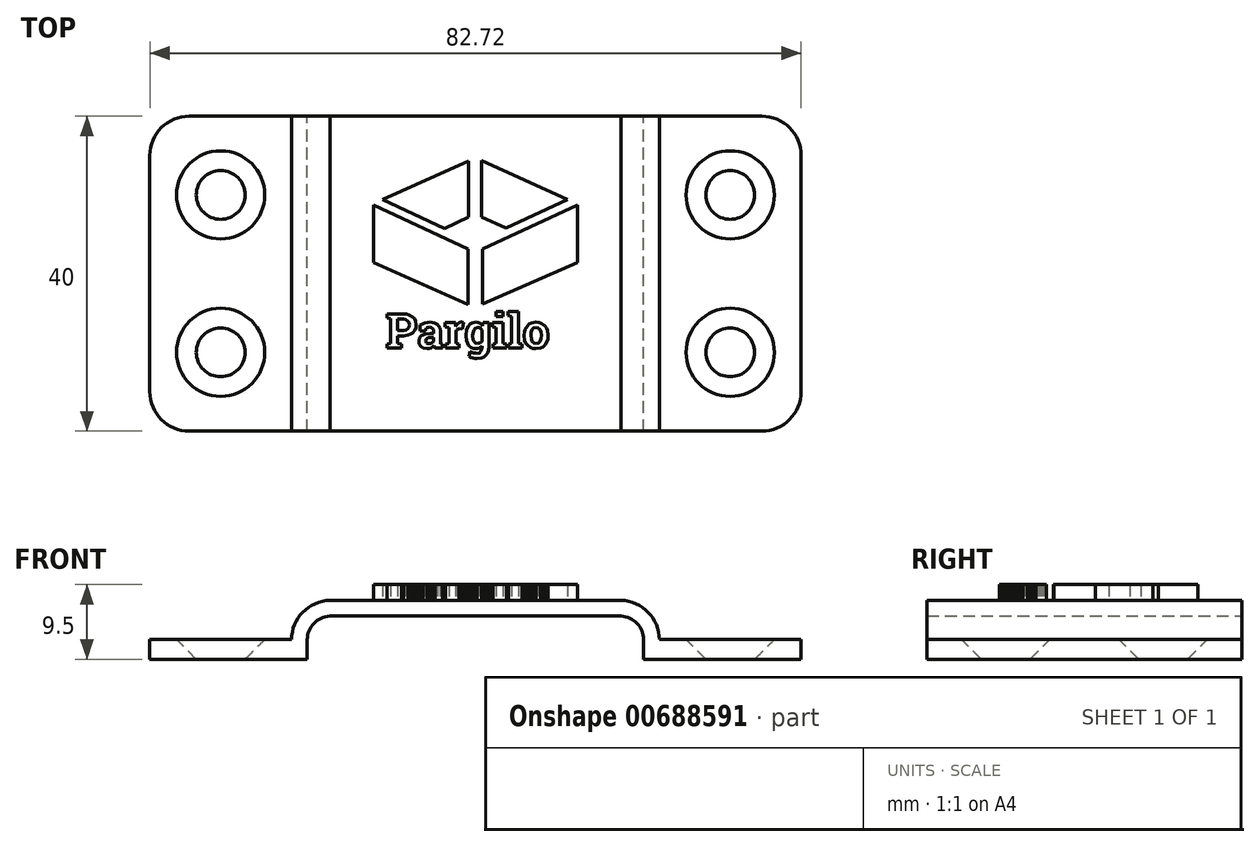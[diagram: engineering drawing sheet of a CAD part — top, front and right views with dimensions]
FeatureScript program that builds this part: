
annotation { "Feature Type Name" : "Feature", "Feature Type Description" : "" }
export const myFeature = defineFeature(function(context is Context, id is Id, definition is map)
    precondition{}
    {
        {
            var Q0;
            Q0=qCreatedBy(makeId("Front.planeOp"),FACE);
            var sketch = newSketch(context, id + "F0", { "sketchPlane" : qUnion([Q0])});
            skLineSegment(sketch, "E0.bottom", {"start": v(-41.36, 2.5) * mm, "end": v(-21.36, 2.5) * mm});
            skLineSegment(sketch, "E0.top", {"start": v(-41.36, 0) * mm, "end": v(-21.36, 0) * mm});
            skLineSegment(sketch, "E0.left", {"start": v(-41.36, 2.5) * mm, "end": v(-41.36, 0) * mm});
            skLineSegment(sketch, "E0.right", {"start": v(-21.36, 2.5) * mm, "end": v(-21.36, 0) * mm});
            skLineSegment(sketch, "E1.bottom", {"start": v(-18.5, 5.5) * mm, "end": v(0, 5.5) * mm});
            skLineSegment(sketch, "E1.top", {"start": v(-18.5, 7.5) * mm, "end": v(0, 7.5) * mm});
            skLineSegment(sketch, "E1.left", {"start": v(-18.5, 5.5) * mm, "end": v(-18.5, 7.5) * mm});
            skLineSegment(sketch, "E1.right", {"start": v(0, 5.5) * mm, "end": v(0, 7.5) * mm});
            skPoint(sketch, "E2", {"position": v(-18.33, 2.48) * mm});
            skArc(sketch, "E3", {"start": v(-18.5, 5.5) * mm, "mid": v(-20.53, 4.57) * mm, "end": v(-21.36, 2.5) * mm});
            skArc(sketch, "E4", {"start": v(-18.5, 7.5) * mm, "mid": v(-21.94, 5.98) * mm, "end": v(-23.36, 2.5) * mm});
            skLineSegment(sketch, "E5.MirrorCS", {"start": v(18.5, 5.5) * mm, "end": v(18.5, 7.5) * mm});
            skLineSegment(sketch, "E6.MirrorCS", {"start": v(21.36, 2.5) * mm, "end": v(21.36, 0) * mm});
            skLineSegment(sketch, "E7.MirrorCS", {"start": v(41.36, 2.5) * mm, "end": v(41.36, 0) * mm});
            skLineSegment(sketch, "E8.MirrorCS", {"start": v(18.5, 7.5) * mm, "end": v(0, 7.5) * mm});
            skArc(sketch, "E9.MirrorCS", {"start": v(18.5, 7.5) * mm, "mid": v(21.94, 5.98) * mm, "end": v(23.36, 2.5) * mm});
            skArc(sketch, "E10.MirrorCS", {"start": v(18.5, 5.5) * mm, "mid": v(20.53, 4.57) * mm, "end": v(21.36, 2.5) * mm});
            skLineSegment(sketch, "E11.MirrorCS", {"start": v(18.5, 5.5) * mm, "end": v(0, 5.5) * mm});
            skLineSegment(sketch, "E12.MirrorCS", {"start": v(41.36, 2.5) * mm, "end": v(21.36, 2.5) * mm});
            skLineSegment(sketch, "E13.MirrorCS", {"start": v(41.36, 0) * mm, "end": v(21.36, 0) * mm});
            skSolve(sketch);
        }
        {
            var Q0;
            Q0 = qSketchRegion(id + "F0", true);
            extrude(context, id + "F1", {"entities" : qUnion([Q0]), "depth" : 40 * mm, "offsetDistance" : 25 * mm});
        }
        {
            var Q0;
            Q0 = qSketchRegion(id + "F0", true);
            extrude(context, id + "F2", {"entities" : qUnion([Q0]), "operationType" : NewBodyOperationType.ADD, "depth" : 27 * mm, "offsetDistance" : 25 * mm});
        }
        {
            var Q0;
            Q0=makeQuery(id+"F1.opExtrude","SWEPT_FACE",FACE,{"disambiguationData":[OSD([sQuery(id+"F0.wireOp",EDGE,"E0.bottom")])]});
            var sketch = newSketch(context, id + "F3", { "sketchPlane" : qUnion([Q0])});
            skPoint(sketch, "E14", {"position": v(-32.36, -10) * mm});
            skPoint(sketch, "E15", {"position": v(-32.36, -30) * mm});
            skPoint(sketch, "E16.MirrorP", {"position": v(32.36, -10) * mm});
            skPoint(sketch, "E17.MirrorP", {"position": v(32.36, -30) * mm});
            skSolve(sketch);
        }
        {
            var Q0;
            Q0=sQuery(id+"F3.wireOp",VERTEX,"E14");
            var Q1;
            Q1=sQuery(id+"F3.wireOp",VERTEX,"E15");
            var Q2;
            Q2=sQuery(id+"F3.wireOp",VERTEX,"E17.MirrorP");
            var Q3;
            Q3=sQuery(id+"F3.wireOp",VERTEX,"E16.MirrorP");
            var Q4;
            Q4=makeQuery(id+"F1.opExtrude","SWEPT_BODY",BODY,{"disambiguationData":[OSD([sQuery(id+"F0.wireOp",EDGE,"E0.bottom"),sQuery(id+"F0.wireOp",EDGE,"E0.top"),sQuery(id+"F0.wireOp",EDGE,"E0.left"),sQuery(id+"F0.wireOp",EDGE,"E0.right"),sQuery(id+"F0.wireOp",EDGE,"E1.bottom"),sQuery(id+"F0.wireOp",EDGE,"E1.top"),sQuery(id+"F0.wireOp",EDGE,"E3"),sQuery(id+"F0.wireOp",EDGE,"E4"),sQuery(id+"F0.wireOp",EDGE,"E6.MirrorCS"),sQuery(id+"F0.wireOp",EDGE,"E7.MirrorCS"),sQuery(id+"F0.wireOp",EDGE,"E8.MirrorCS"),sQuery(id+"F0.wireOp",EDGE,"E9.MirrorCS"),sQuery(id+"F0.wireOp",EDGE,"E10.MirrorCS"),sQuery(id+"F0.wireOp",EDGE,"E11.MirrorCS"),sQuery(id+"F0.wireOp",EDGE,"E12.MirrorCS"),sQuery(id+"F0.wireOp",EDGE,"E13.MirrorCS")])]});
            hole(context, id + "F4", {"style" : HoleStyle.C_SINK, "endStyle" : HoleEndStyle.THROUGH, "standardTappedOrClearance" : lookupTablePath({ "standard" : "ISO", "size" : "5", "type" : "Drilled" }), "standardBlindInLast" : lookupTablePath({ "standard" : "ISO", "size" : "5", "type" : "Drilled" }), "holeDiameter" : 5 * mm, "cSinkDiameter" : 11.2 * mm, "cSinkAngle" : 90 * degree, "majorDiameter" : 5 * mm, "isTappedThrough" : true, "tappedDepth" : 12 * mm, "tapClearance" : 3, "locations" : qUnion([Q0, Q1, Q2, Q3]), "scope" : qUnion([Q4])});
        }
        {
            var Q0;
            Q0=makeQuery(id+"F1.opExtrude","CAP_EDGE",EDGE,{"disambiguationData":[OSD([sQuery(id+"F0.wireOp",EDGE,"E0.left")])],"isStart":false});
            var Q1;
            Q1=makeQuery(id+"F1.opExtrude","CAP_EDGE",EDGE,{"disambiguationData":[OSD([sQuery(id+"F0.wireOp",EDGE,"E7.MirrorCS")])],"isStart":false});
            var Q2;
            Q2=makeQuery(id+"F1.opExtrude","CAP_EDGE",EDGE,{"disambiguationData":[OSD([sQuery(id+"F0.wireOp",EDGE,"E7.MirrorCS")])],"isStart":true});
            var Q3;
            Q3=makeQuery(id+"F1.opExtrude","CAP_EDGE",EDGE,{"disambiguationData":[OSD([sQuery(id+"F0.wireOp",EDGE,"E0.left")])],"isStart":true});
            fillet(context, id + "F5", {"entities" : qUnion([Q0, Q1, Q2, Q3]), "radius" : 5 * mm, "tangentPropagation" : true, "allowEdgeOverflow" : false});
        }
        {
            var Q0;
            Q0=makeQuery(id+"F1.opExtrude","SWEPT_FACE",FACE,{"disambiguationData":[OSD([sQuery(id+"F0.wireOp",EDGE,"E1.top"),sQuery(id+"F0.wireOp",EDGE,"E8.MirrorCS")])]});
            var sketch = newSketch(context, id + "F6", { "sketchPlane" : qUnion([Q0])});
            skLineSegment(sketch, "E18", {"start": v(-12.95, -11.28) * mm, "end": v(-12.95, -18.58) * mm});
            skLineSegment(sketch, "E19", {"start": v(7.05, -27.83) * mm, "end": v(7.05, -27.9) * mm});
            skLineSegment(sketch, "E20", {"start": v(7.2, -27.12) * mm, "end": v(7.08, -27.48) * mm});
            skLineSegment(sketch, "E21", {"start": v(7.08, -27.48) * mm, "end": v(7.05, -27.83) * mm});
            skLineSegment(sketch, "E22", {"start": v(7.7, -26.85) * mm, "end": v(7.38, -26.94) * mm});
            skLineSegment(sketch, "E23", {"start": v(7.38, -26.94) * mm, "end": v(7.2, -27.12) * mm});
            skLineSegment(sketch, "E24", {"start": v(8.2, -27.12) * mm, "end": v(7.97, -26.9) * mm});
            skLineSegment(sketch, "E25", {"start": v(7.97, -26.9) * mm, "end": v(7.7, -26.85) * mm});
            skLineSegment(sketch, "E26", {"start": v(8.36, -27.83) * mm, "end": v(8.31, -27.4) * mm});
            skLineSegment(sketch, "E27", {"start": v(8.31, -27.4) * mm, "end": v(8.2, -27.12) * mm});
            skLineSegment(sketch, "E28", {"start": v(8.36, -27.9) * mm, "end": v(8.36, -27.83) * mm});
            skLineSegment(sketch, "E29", {"start": v(8.2, -28.6) * mm, "end": v(8.33, -28.25) * mm});
            skLineSegment(sketch, "E30", {"start": v(8.33, -28.25) * mm, "end": v(8.36, -27.9) * mm});
            skLineSegment(sketch, "E31", {"start": v(7.71, -28.87) * mm, "end": v(8.03, -28.79) * mm});
            skLineSegment(sketch, "E32", {"start": v(8.03, -28.79) * mm, "end": v(8.2, -28.6) * mm});
            skLineSegment(sketch, "E33", {"start": v(7.2, -28.6) * mm, "end": v(7.44, -28.82) * mm});
            skLineSegment(sketch, "E34", {"start": v(7.44, -28.82) * mm, "end": v(7.71, -28.87) * mm});
            skLineSegment(sketch, "E35", {"start": v(7.05, -27.9) * mm, "end": v(7.1, -28.33) * mm});
            skLineSegment(sketch, "E36", {"start": v(7.1, -28.33) * mm, "end": v(7.2, -28.6) * mm});
            skLineSegment(sketch, "E37", {"start": v(6.18, -27.9) * mm, "end": v(6.18, -27.83) * mm});
            skLineSegment(sketch, "E38", {"start": v(6.58, -29.08) * mm, "end": v(6.39, -28.8) * mm});
            skLineSegment(sketch, "E39", {"start": v(6.39, -28.8) * mm, "end": v(6.25, -28.48) * mm});
            skLineSegment(sketch, "E40", {"start": v(6.25, -28.48) * mm, "end": v(6.18, -27.9) * mm});
            skLineSegment(sketch, "E41", {"start": v(7.71, -29.54) * mm, "end": v(7.33, -29.5) * mm});
            skLineSegment(sketch, "E42", {"start": v(7.33, -29.5) * mm, "end": v(7, -29.4) * mm});
            skLineSegment(sketch, "E43", {"start": v(7, -29.4) * mm, "end": v(6.58, -29.08) * mm});
            skLineSegment(sketch, "E44", {"start": v(8.83, -29.08) * mm, "end": v(8.58, -29.3) * mm});
            skLineSegment(sketch, "E45", {"start": v(8.58, -29.3) * mm, "end": v(8.28, -29.45) * mm});
            skLineSegment(sketch, "E46", {"start": v(8.28, -29.45) * mm, "end": v(7.71, -29.54) * mm});
            skLineSegment(sketch, "E47", {"start": v(9.24, -27.9) * mm, "end": v(9.2, -28.28) * mm});
            skLineSegment(sketch, "E48", {"start": v(9.2, -28.28) * mm, "end": v(9.11, -28.62) * mm});
            skLineSegment(sketch, "E49", {"start": v(9.11, -28.62) * mm, "end": v(8.83, -29.08) * mm});
            skLineSegment(sketch, "E50", {"start": v(9.24, -27.83) * mm, "end": v(9.24, -27.9) * mm});
            skLineSegment(sketch, "E51", {"start": v(8.83, -26.64) * mm, "end": v(9.03, -26.92) * mm});
            skLineSegment(sketch, "E52", {"start": v(9.03, -26.92) * mm, "end": v(9.16, -27.24) * mm});
            skLineSegment(sketch, "E53", {"start": v(9.16, -27.24) * mm, "end": v(9.24, -27.83) * mm});
            skLineSegment(sketch, "E54", {"start": v(7.7, -26.17) * mm, "end": v(8.08, -26.21) * mm});
            skLineSegment(sketch, "E55", {"start": v(8.08, -26.21) * mm, "end": v(8.41, -26.32) * mm});
            skLineSegment(sketch, "E56", {"start": v(8.41, -26.32) * mm, "end": v(8.83, -26.64) * mm});
            skLineSegment(sketch, "E57", {"start": v(6.58, -26.64) * mm, "end": v(6.83, -26.42) * mm});
            skLineSegment(sketch, "E58", {"start": v(6.83, -26.42) * mm, "end": v(7.13, -26.26) * mm});
            skLineSegment(sketch, "E59", {"start": v(7.13, -26.26) * mm, "end": v(7.7, -26.17) * mm});
            skLineSegment(sketch, "E60", {"start": v(6.18, -27.83) * mm, "end": v(6.2, -27.44) * mm});
            skLineSegment(sketch, "E61", {"start": v(6.2, -27.44) * mm, "end": v(6.3, -27.1) * mm});
            skLineSegment(sketch, "E62", {"start": v(6.3, -27.1) * mm, "end": v(6.58, -26.64) * mm});
            skLineSegment(sketch, "E63", {"start": v(4.6, -25.42) * mm, "end": v(4.12, -25.33) * mm});
            skLineSegment(sketch, "E64", {"start": v(4.6, -28.86) * mm, "end": v(4.6, -25.42) * mm});
            skLineSegment(sketch, "E65", {"start": v(4.17, -28.95) * mm, "end": v(4.6, -28.86) * mm});
            skLineSegment(sketch, "E66", {"start": v(4.17, -29.48) * mm, "end": v(4.17, -28.95) * mm});
            skLineSegment(sketch, "E67", {"start": v(5.9, -29.48) * mm, "end": v(4.17, -29.48) * mm});
            skLineSegment(sketch, "E68", {"start": v(5.9, -28.95) * mm, "end": v(5.9, -29.48) * mm});
            skLineSegment(sketch, "E69", {"start": v(5.47, -28.86) * mm, "end": v(5.9, -28.95) * mm});
            skLineSegment(sketch, "E70", {"start": v(5.47, -24.8) * mm, "end": v(5.47, -28.86) * mm});
            skLineSegment(sketch, "E71", {"start": v(4.12, -24.8) * mm, "end": v(5.47, -24.8) * mm});
            skLineSegment(sketch, "E72", {"start": v(4.12, -25.33) * mm, "end": v(4.12, -24.8) * mm});
            skLineSegment(sketch, "E73", {"start": v(3.5, -24.8) * mm, "end": v(3.5, -25.46) * mm});
            skLineSegment(sketch, "E74", {"start": v(2.63, -24.8) * mm, "end": v(3.5, -24.8) * mm});
            skLineSegment(sketch, "E75", {"start": v(2.63, -25.46) * mm, "end": v(2.63, -24.8) * mm});
            skLineSegment(sketch, "E76", {"start": v(3.5, -25.46) * mm, "end": v(2.63, -25.46) * mm});
            skLineSegment(sketch, "E77", {"start": v(2.21, -29.48) * mm, "end": v(2.21, -28.95) * mm});
            skLineSegment(sketch, "E78", {"start": v(3.93, -29.48) * mm, "end": v(2.21, -29.48) * mm});
            skLineSegment(sketch, "E79", {"start": v(3.93, -28.95) * mm, "end": v(3.93, -29.48) * mm});
            skLineSegment(sketch, "E80", {"start": v(3.5, -28.86) * mm, "end": v(3.93, -28.95) * mm});
            skLineSegment(sketch, "E81", {"start": v(3.5, -26.24) * mm, "end": v(3.5, -28.86) * mm});
            skLineSegment(sketch, "E82", {"start": v(2.17, -26.24) * mm, "end": v(3.5, -26.24) * mm});
            skLineSegment(sketch, "E83", {"start": v(2.17, -26.76) * mm, "end": v(2.17, -26.24) * mm});
            skLineSegment(sketch, "E84", {"start": v(2.63, -26.85) * mm, "end": v(2.17, -26.76) * mm});
            skLineSegment(sketch, "E85", {"start": v(2.63, -28.86) * mm, "end": v(2.63, -26.85) * mm});
            skLineSegment(sketch, "E86", {"start": v(2.21, -28.95) * mm, "end": v(2.63, -28.86) * mm});
            skLineSegment(sketch, "E87", {"start": v(-0.34, -27.88) * mm, "end": v(-0.34, -27.95) * mm});
            skLineSegment(sketch, "E88", {"start": v(-0.2, -27.14) * mm, "end": v(-0.31, -27.51) * mm});
            skLineSegment(sketch, "E89", {"start": v(-0.31, -27.51) * mm, "end": v(-0.34, -27.88) * mm});
            skLineSegment(sketch, "E90", {"start": v(0.28, -26.86) * mm, "end": v(-0.03, -26.95) * mm});
            skLineSegment(sketch, "E91", {"start": v(-0.03, -26.95) * mm, "end": v(-0.2, -27.14) * mm});
            skLineSegment(sketch, "E92", {"start": v(0.61, -26.94) * mm, "end": v(0.44, -26.87) * mm});
            skLineSegment(sketch, "E93", {"start": v(0.44, -26.87) * mm, "end": v(0.28, -26.86) * mm});
            skLineSegment(sketch, "E94", {"start": v(0.84, -27.16) * mm, "end": v(0.72, -27.02) * mm});
            skLineSegment(sketch, "E95", {"start": v(0.72, -27.02) * mm, "end": v(0.61, -26.94) * mm});
            skLineSegment(sketch, "E96", {"start": v(0.84, -28.57) * mm, "end": v(0.84, -27.16) * mm});
            skLineSegment(sketch, "E97", {"start": v(0.61, -28.79) * mm, "end": v(0.75, -28.68) * mm});
            skLineSegment(sketch, "E98", {"start": v(0.75, -28.68) * mm, "end": v(0.84, -28.57) * mm});
            skLineSegment(sketch, "E99", {"start": v(0.27, -28.86) * mm, "end": v(0.48, -28.84) * mm});
            skLineSegment(sketch, "E100", {"start": v(0.48, -28.84) * mm, "end": v(0.61, -28.79) * mm});
            skLineSegment(sketch, "E101", {"start": v(-0.2, -28.62) * mm, "end": v(0.02, -28.81) * mm});
            skLineSegment(sketch, "E102", {"start": v(0.02, -28.81) * mm, "end": v(0.27, -28.86) * mm});
            skLineSegment(sketch, "E103", {"start": v(-0.34, -27.95) * mm, "end": v(-0.3, -28.37) * mm});
            skLineSegment(sketch, "E104", {"start": v(-0.3, -28.37) * mm, "end": v(-0.2, -28.62) * mm});
            skLineSegment(sketch, "E105", {"start": v(-4.15, -28.95) * mm, "end": v(-4.15, -29.48) * mm});
            skLineSegment(sketch, "E106", {"start": v(-4.42, -28.92) * mm, "end": v(-4.15, -28.95) * mm});
            skLineSegment(sketch, "E107", {"start": v(-4.43, -28.8) * mm, "end": v(-4.43, -28.86) * mm});
            skLineSegment(sketch, "E108", {"start": v(-4.43, -28.86) * mm, "end": v(-4.42, -28.92) * mm});
            skLineSegment(sketch, "E109", {"start": v(-4.43, -28.65) * mm, "end": v(-4.43, -28.73) * mm});
            skLineSegment(sketch, "E110", {"start": v(-4.43, -28.73) * mm, "end": v(-4.43, -28.8) * mm});
            skLineSegment(sketch, "E111", {"start": v(-4.43, -27.31) * mm, "end": v(-4.43, -28.65) * mm});
            skLineSegment(sketch, "E112", {"start": v(-4.8, -26.47) * mm, "end": v(-4.5, -26.88) * mm});
            skLineSegment(sketch, "E113", {"start": v(-4.5, -26.88) * mm, "end": v(-4.43, -27.31) * mm});
            skLineSegment(sketch, "E114", {"start": v(-5.79, -26.17) * mm, "end": v(-5.18, -26.27) * mm});
            skLineSegment(sketch, "E115", {"start": v(-5.18, -26.27) * mm, "end": v(-4.8, -26.47) * mm});
            skLineSegment(sketch, "E116", {"start": v(-6.46, -26.29) * mm, "end": v(-6.1, -26.2) * mm});
            skLineSegment(sketch, "E117", {"start": v(-6.1, -26.2) * mm, "end": v(-5.79, -26.17) * mm});
            skLineSegment(sketch, "E118", {"start": v(-7.01, -26.56) * mm, "end": v(-6.72, -26.4) * mm});
            skLineSegment(sketch, "E119", {"start": v(-6.72, -26.4) * mm, "end": v(-6.46, -26.29) * mm});
            skLineSegment(sketch, "E120", {"start": v(-7.02, -27.28) * mm, "end": v(-7.01, -26.56) * mm});
            skLineSegment(sketch, "E121", {"start": v(-4.15, -29.48) * mm, "end": v(-5.16, -29.48) * mm});
            skLineSegment(sketch, "E122", {"start": v(-5.92, -28.9) * mm, "end": v(-5.71, -28.87) * mm});
            skLineSegment(sketch, "E123", {"start": v(-5.71, -28.87) * mm, "end": v(-5.56, -28.8) * mm});
            skLineSegment(sketch, "E124", {"start": v(-5.56, -28.8) * mm, "end": v(-5.4, -28.7) * mm});
            skLineSegment(sketch, "E125", {"start": v(-5.4, -28.7) * mm, "end": v(-5.3, -28.6) * mm});
            skLineSegment(sketch, "E126", {"start": v(-5.3, -28.6) * mm, "end": v(-5.3, -28.1) * mm});
            skLineSegment(sketch, "E127", {"start": v(-5.3, -28.1) * mm, "end": v(-5.76, -28.1) * mm});
            skLineSegment(sketch, "E128", {"start": v(-5.76, -28.1) * mm, "end": v(-6.03, -28.14) * mm});
            skLineSegment(sketch, "E129", {"start": v(-6.03, -28.14) * mm, "end": v(-6.18, -28.23) * mm});
            skLineSegment(sketch, "E130", {"start": v(-6.18, -28.23) * mm, "end": v(-6.3, -28.4) * mm});
            skLineSegment(sketch, "E131", {"start": v(-6.3, -28.4) * mm, "end": v(-6.32, -28.54) * mm});
            skLineSegment(sketch, "E132", {"start": v(-6.32, -28.54) * mm, "end": v(-6.29, -28.7) * mm});
            skLineSegment(sketch, "E133", {"start": v(-6.29, -28.7) * mm, "end": v(-6.22, -28.8) * mm});
            skLineSegment(sketch, "E134", {"start": v(0.78, -12.83) * mm, "end": v(3.9, -14.22) * mm});
            skLineSegment(sketch, "E135", {"start": v(-0.67, -29.92) * mm, "end": v(-0.43, -30.01) * mm});
            skLineSegment(sketch, "E136", {"start": v(-0.43, -30.01) * mm, "end": v(-0.25, -30.07) * mm});
            skLineSegment(sketch, "E137", {"start": v(3.9, -14.22) * mm, "end": v(11.7, -10.6) * mm});
            skLineSegment(sketch, "E138", {"start": v(-0.25, -30.07) * mm, "end": v(0, -30.1) * mm});
            skLineSegment(sketch, "E139", {"start": v(0, -30.1) * mm, "end": v(0.2, -30.12) * mm});
            skLineSegment(sketch, "E140", {"start": v(11.7, -10.6) * mm, "end": v(0.78, -5.6) * mm});
            skLineSegment(sketch, "E141", {"start": v(0.2, -30.12) * mm, "end": v(0.5, -30.06) * mm});
            skLineSegment(sketch, "E142", {"start": v(0.5, -30.06) * mm, "end": v(0.68, -29.92) * mm});
            skLineSegment(sketch, "E143", {"start": v(-9.14, -25.11) * mm, "end": v(-8.75, -25.14) * mm});
            skLineSegment(sketch, "E144", {"start": v(-8.75, -25.14) * mm, "end": v(-8.4, -25.23) * mm});
            skLineSegment(sketch, "E145", {"start": v(-8.4, -25.23) * mm, "end": v(-7.96, -25.5) * mm});
            skLineSegment(sketch, "E146", {"start": v(-0.88, -29.1) * mm, "end": v(-1.15, -28.52) * mm});
            skLineSegment(sketch, "E147", {"start": v(-1.15, -28.52) * mm, "end": v(-1.22, -27.95) * mm});
            skLineSegment(sketch, "E148", {"start": v(-7.96, -25.5) * mm, "end": v(-7.75, -25.73) * mm});
            skLineSegment(sketch, "E149", {"start": v(-7.75, -25.73) * mm, "end": v(-7.61, -26) * mm});
            skLineSegment(sketch, "E150", {"start": v(-7.61, -26) * mm, "end": v(-7.53, -26.5) * mm});
            skLineSegment(sketch, "E151", {"start": v(-1.22, -27.95) * mm, "end": v(-1.22, -27.88) * mm});
            skLineSegment(sketch, "E152", {"start": v(-7.53, -26.5) * mm, "end": v(-7.56, -26.84) * mm});
            skLineSegment(sketch, "E153", {"start": v(-7.56, -26.84) * mm, "end": v(-7.66, -27.13) * mm});
            skLineSegment(sketch, "E154", {"start": v(-7.66, -27.13) * mm, "end": v(-7.96, -27.52) * mm});
            skLineSegment(sketch, "E155", {"start": v(-7.96, -27.52) * mm, "end": v(-8.23, -27.7) * mm});
            skLineSegment(sketch, "E156", {"start": v(-8.23, -27.7) * mm, "end": v(-8.55, -27.82) * mm});
            skLineSegment(sketch, "E157", {"start": v(-8.55, -27.82) * mm, "end": v(-9.14, -27.9) * mm});
            skLineSegment(sketch, "E158", {"start": v(-9.14, -27.9) * mm, "end": v(-9.88, -27.9) * mm});
            skLineSegment(sketch, "E159", {"start": v(-9.88, -27.9) * mm, "end": v(-9.88, -28.86) * mm});
            skLineSegment(sketch, "E160", {"start": v(-9.88, -28.86) * mm, "end": v(-9.42, -28.95) * mm});
            skLineSegment(sketch, "E161", {"start": v(-9.42, -28.95) * mm, "end": v(-9.42, -29.48) * mm});
            skLineSegment(sketch, "E162", {"start": v(-9.42, -29.48) * mm, "end": v(-11.22, -29.48) * mm});
            skLineSegment(sketch, "E163", {"start": v(-11.22, -29.48) * mm, "end": v(-11.22, -28.95) * mm});
            skLineSegment(sketch, "E164", {"start": v(-11.22, -28.95) * mm, "end": v(-10.76, -28.86) * mm});
            skLineSegment(sketch, "E165", {"start": v(-10.76, -28.86) * mm, "end": v(-10.76, -25.73) * mm});
            skLineSegment(sketch, "E166", {"start": v(-10.76, -25.73) * mm, "end": v(-11.22, -25.64) * mm});
            skLineSegment(sketch, "E167", {"start": v(-11.22, -25.64) * mm, "end": v(-11.22, -25.11) * mm});
            skLineSegment(sketch, "E168", {"start": v(-11.22, -25.11) * mm, "end": v(-10.76, -25.11) * mm});
            skLineSegment(sketch, "E169", {"start": v(-10.76, -25.11) * mm, "end": v(-9.14, -25.11) * mm});
            skLineSegment(sketch, "E170", {"start": v(-9.88, -27.22) * mm, "end": v(-9.14, -27.22) * mm});
            skLineSegment(sketch, "E171", {"start": v(-7.2, -28.58) * mm, "end": v(-7.08, -28.13) * mm});
            skLineSegment(sketch, "E172", {"start": v(-7.08, -28.13) * mm, "end": v(-6.83, -27.87) * mm});
            skLineSegment(sketch, "E173", {"start": v(-6.83, -27.87) * mm, "end": v(-6.31, -27.67) * mm});
            skLineSegment(sketch, "E174", {"start": v(-6.31, -27.67) * mm, "end": v(-5.76, -27.62) * mm});
            skLineSegment(sketch, "E175", {"start": v(-5.76, -27.62) * mm, "end": v(-5.3, -27.62) * mm});
            skLineSegment(sketch, "E176", {"start": v(-5.3, -27.62) * mm, "end": v(-5.3, -27.3) * mm});
            skLineSegment(sketch, "E177", {"start": v(-5.3, -27.3) * mm, "end": v(-5.35, -27.08) * mm});
            skLineSegment(sketch, "E178", {"start": v(-5.35, -27.08) * mm, "end": v(-5.44, -26.94) * mm});
            skLineSegment(sketch, "E179", {"start": v(-5.44, -26.94) * mm, "end": v(-5.64, -26.84) * mm});
            skLineSegment(sketch, "E180", {"start": v(-5.64, -26.84) * mm, "end": v(-5.84, -26.81) * mm});
            skLineSegment(sketch, "E181", {"start": v(0.78, -5.6) * mm, "end": v(0.78, -12.83) * mm});
            skLineSegment(sketch, "E182", {"start": v(-0.83, -30.54) * mm, "end": v(-0.67, -29.92) * mm});
            skLineSegment(sketch, "E183", {"start": v(-6.36, -27.28) * mm, "end": v(-7.02, -27.28) * mm});
            skLineSegment(sketch, "E184", {"start": v(-0.89, -5.72) * mm, "end": v(-11.81, -10.6) * mm});
            skLineSegment(sketch, "E185", {"start": v(-0.32, -30.72) * mm, "end": v(-0.62, -30.63) * mm});
            skLineSegment(sketch, "E186", {"start": v(-0.62, -30.63) * mm, "end": v(-0.83, -30.54) * mm});
            skLineSegment(sketch, "E187", {"start": v(-6.3, -26.93) * mm, "end": v(-6.36, -27.28) * mm});
            skLineSegment(sketch, "E188", {"start": v(-0.89, -12.83) * mm, "end": v(-0.89, -5.72) * mm});
            skLineSegment(sketch, "E189", {"start": v(0.2, -30.8) * mm, "end": v(-0.08, -30.77) * mm});
            skLineSegment(sketch, "E190", {"start": v(-0.08, -30.77) * mm, "end": v(-0.32, -30.72) * mm});
            skLineSegment(sketch, "E191", {"start": v(-6.11, -26.85) * mm, "end": v(-6.23, -26.9) * mm});
            skLineSegment(sketch, "E192", {"start": v(-6.23, -26.9) * mm, "end": v(-6.3, -26.93) * mm});
            skLineSegment(sketch, "E193", {"start": v(-3.96, -14.25) * mm, "end": v(-0.89, -12.83) * mm});
            skLineSegment(sketch, "E194", {"start": v(1.31, -30.4) * mm, "end": v(1.06, -30.6) * mm});
            skLineSegment(sketch, "E195", {"start": v(1.06, -30.6) * mm, "end": v(0.76, -30.72) * mm});
            skLineSegment(sketch, "E196", {"start": v(0.76, -30.72) * mm, "end": v(0.2, -30.8) * mm});
            skLineSegment(sketch, "E197", {"start": v(-5.84, -26.81) * mm, "end": v(-6, -26.82) * mm});
            skLineSegment(sketch, "E198", {"start": v(-6, -26.82) * mm, "end": v(-6.11, -26.85) * mm});
            skLineSegment(sketch, "E199", {"start": v(-6.92, -29.28) * mm, "end": v(-7.14, -28.93) * mm});
            skLineSegment(sketch, "E200", {"start": v(-7.14, -28.93) * mm, "end": v(-7.2, -28.58) * mm});
            skLineSegment(sketch, "E201", {"start": v(-6.16, -29.54) * mm, "end": v(-6.63, -29.46) * mm});
            skLineSegment(sketch, "E202", {"start": v(-6.63, -29.46) * mm, "end": v(-6.92, -29.28) * mm});
            skLineSegment(sketch, "E203", {"start": v(-5.65, -29.43) * mm, "end": v(-5.92, -29.52) * mm});
            skLineSegment(sketch, "E204", {"start": v(-5.92, -29.52) * mm, "end": v(-6.16, -29.54) * mm});
            skLineSegment(sketch, "E205", {"start": v(-5.27, -29.14) * mm, "end": v(-5.46, -29.32) * mm});
            skLineSegment(sketch, "E206", {"start": v(-5.46, -29.32) * mm, "end": v(-5.65, -29.43) * mm});
            skLineSegment(sketch, "E207", {"start": v(-5.23, -29.31) * mm, "end": v(-5.25, -29.22) * mm});
            skLineSegment(sketch, "E208", {"start": v(-5.25, -29.22) * mm, "end": v(-5.27, -29.14) * mm});
            skLineSegment(sketch, "E209", {"start": v(-5.16, -29.48) * mm, "end": v(-5.2, -29.39) * mm});
            skLineSegment(sketch, "E210", {"start": v(-5.2, -29.39) * mm, "end": v(-5.23, -29.31) * mm});
            skLineSegment(sketch, "E211", {"start": v(-9.88, -25.79) * mm, "end": v(-9.88, -27.22) * mm});
            skLineSegment(sketch, "E212", {"start": v(-9.14, -25.79) * mm, "end": v(-9.88, -25.79) * mm});
            skLineSegment(sketch, "E213", {"start": v(-8.6, -26) * mm, "end": v(-8.86, -25.83) * mm});
            skLineSegment(sketch, "E214", {"start": v(-8.86, -25.83) * mm, "end": v(-9.14, -25.79) * mm});
            skLineSegment(sketch, "E215", {"start": v(-8.4, -26.51) * mm, "end": v(-8.46, -26.2) * mm});
            skLineSegment(sketch, "E216", {"start": v(-8.46, -26.2) * mm, "end": v(-8.6, -26) * mm});
            skLineSegment(sketch, "E217", {"start": v(-8.6, -27.02) * mm, "end": v(-8.44, -26.76) * mm});
            skLineSegment(sketch, "E218", {"start": v(-8.44, -26.76) * mm, "end": v(-8.4, -26.51) * mm});
            skLineSegment(sketch, "E219", {"start": v(-9.14, -27.22) * mm, "end": v(-8.8, -27.16) * mm});
            skLineSegment(sketch, "E220", {"start": v(-8.8, -27.16) * mm, "end": v(-8.6, -27.02) * mm});
            skLineSegment(sketch, "E221", {"start": v(-11.81, -10.6) * mm, "end": v(-3.96, -14.25) * mm});
            skLineSegment(sketch, "E222", {"start": v(1.71, -29.38) * mm, "end": v(1.68, -29.72) * mm});
            skLineSegment(sketch, "E223", {"start": v(1.68, -29.72) * mm, "end": v(1.59, -30.02) * mm});
            skLineSegment(sketch, "E224", {"start": v(1.59, -30.02) * mm, "end": v(1.31, -30.4) * mm});
            skLineSegment(sketch, "E225", {"start": v(12.95, -18.6) * mm, "end": v(0.88, -23.88) * mm});
            skLineSegment(sketch, "E226", {"start": v(1.71, -26.24) * mm, "end": v(1.71, -29.38) * mm});
            skLineSegment(sketch, "E227", {"start": v(12.95, -11.28) * mm, "end": v(12.95, -18.6) * mm});
            skLineSegment(sketch, "E228", {"start": v(0.95, -26.24) * mm, "end": v(1.71, -26.24) * mm});
            skLineSegment(sketch, "E229", {"start": v(0.88, -16.87) * mm, "end": v(12.95, -11.28) * mm});
            skLineSegment(sketch, "E230", {"start": v(0.89, -26.64) * mm, "end": v(0.95, -26.24) * mm});
            skLineSegment(sketch, "E231", {"start": v(0.88, -23.88) * mm, "end": v(0.88, -16.87) * mm});
            skLineSegment(sketch, "E232", {"start": v(0.54, -26.3) * mm, "end": v(0.75, -26.46) * mm});
            skLineSegment(sketch, "E233", {"start": v(0.75, -26.46) * mm, "end": v(0.89, -26.64) * mm});
            skLineSegment(sketch, "E234", {"start": v(-0.92, -16.87) * mm, "end": v(-12.95, -11.28) * mm});
            skLineSegment(sketch, "E235", {"start": v(0.06, -26.17) * mm, "end": v(0.34, -26.21) * mm});
            skLineSegment(sketch, "E236", {"start": v(0.34, -26.21) * mm, "end": v(0.54, -26.3) * mm});
            skLineSegment(sketch, "E237", {"start": v(-0.92, -23.95) * mm, "end": v(-0.92, -16.87) * mm});
            skLineSegment(sketch, "E238", {"start": v(-0.88, -26.65) * mm, "end": v(-0.67, -26.42) * mm});
            skLineSegment(sketch, "E239", {"start": v(-0.67, -26.42) * mm, "end": v(-0.42, -26.27) * mm});
            skLineSegment(sketch, "E240", {"start": v(-0.42, -26.27) * mm, "end": v(0.06, -26.17) * mm});
            skLineSegment(sketch, "E241", {"start": v(-12.95, -18.58) * mm, "end": v(-0.92, -23.95) * mm});
            skLineSegment(sketch, "E242", {"start": v(-1.22, -27.88) * mm, "end": v(-1.11, -27.12) * mm});
            skLineSegment(sketch, "E243", {"start": v(-1.11, -27.12) * mm, "end": v(-0.88, -26.65) * mm});
            skLineSegment(sketch, "E244", {"start": v(0.05, -29.54) * mm, "end": v(-0.26, -29.5) * mm});
            skLineSegment(sketch, "E245", {"start": v(-0.26, -29.5) * mm, "end": v(-0.54, -29.4) * mm});
            skLineSegment(sketch, "E246", {"start": v(-0.54, -29.4) * mm, "end": v(-0.88, -29.1) * mm});
            skLineSegment(sketch, "E247", {"start": v(0.5, -29.45) * mm, "end": v(0.26, -29.52) * mm});
            skLineSegment(sketch, "E248", {"start": v(0.26, -29.52) * mm, "end": v(0.05, -29.54) * mm});
            skLineSegment(sketch, "E249", {"start": v(0.84, -29.17) * mm, "end": v(0.66, -29.35) * mm});
            skLineSegment(sketch, "E250", {"start": v(0.66, -29.35) * mm, "end": v(0.5, -29.45) * mm});
            skLineSegment(sketch, "E251", {"start": v(0.84, -29.38) * mm, "end": v(0.84, -29.17) * mm});
            skLineSegment(sketch, "E252", {"start": v(0.68, -29.92) * mm, "end": v(0.8, -29.66) * mm});
            skLineSegment(sketch, "E253", {"start": v(0.8, -29.66) * mm, "end": v(0.84, -29.38) * mm});
            skLineSegment(sketch, "E254", {"start": v(-3.79, -29.48) * mm, "end": v(-3.79, -28.95) * mm});
            skLineSegment(sketch, "E255", {"start": v(-2.07, -29.48) * mm, "end": v(-3.79, -29.48) * mm});
            skLineSegment(sketch, "E256", {"start": v(-2.07, -28.95) * mm, "end": v(-2.07, -29.48) * mm});
            skLineSegment(sketch, "E257", {"start": v(-2.5, -28.86) * mm, "end": v(-2.07, -28.95) * mm});
            skLineSegment(sketch, "E258", {"start": v(-2.5, -27.29) * mm, "end": v(-2.5, -28.86) * mm});
            skLineSegment(sketch, "E259", {"start": v(-2.3, -27.07) * mm, "end": v(-2.42, -27.18) * mm});
            skLineSegment(sketch, "E260", {"start": v(-2.42, -27.18) * mm, "end": v(-2.5, -27.29) * mm});
            skLineSegment(sketch, "E261", {"start": v(-1.98, -27) * mm, "end": v(-2.18, -27.02) * mm});
            skLineSegment(sketch, "E262", {"start": v(-2.18, -27.02) * mm, "end": v(-2.3, -27.07) * mm});
            skLineSegment(sketch, "E263", {"start": v(-1.62, -27) * mm, "end": v(-1.98, -27) * mm});
            skLineSegment(sketch, "E264", {"start": v(-1.53, -26.21) * mm, "end": v(-1.62, -27) * mm});
            skLineSegment(sketch, "E265", {"start": v(-1.66, -26.19) * mm, "end": v(-1.58, -26.2) * mm});
            skLineSegment(sketch, "E266", {"start": v(-1.58, -26.2) * mm, "end": v(-1.53, -26.21) * mm});
            skLineSegment(sketch, "E267", {"start": v(-1.8, -26.17) * mm, "end": v(-1.72, -26.18) * mm});
            skLineSegment(sketch, "E268", {"start": v(-1.72, -26.18) * mm, "end": v(-1.66, -26.19) * mm});
            skLineSegment(sketch, "E269", {"start": v(-2.22, -26.32) * mm, "end": v(-2, -26.2) * mm});
            skLineSegment(sketch, "E270", {"start": v(-2, -26.2) * mm, "end": v(-1.8, -26.17) * mm});
            skLineSegment(sketch, "E271", {"start": v(-2.51, -26.7) * mm, "end": v(-2.37, -26.46) * mm});
            skLineSegment(sketch, "E272", {"start": v(-2.37, -26.46) * mm, "end": v(-2.22, -26.32) * mm});
            skLineSegment(sketch, "E273", {"start": v(-2.55, -26.24) * mm, "end": v(-2.51, -26.7) * mm});
            skLineSegment(sketch, "E274", {"start": v(-3.83, -26.24) * mm, "end": v(-2.55, -26.24) * mm});
            skLineSegment(sketch, "E275", {"start": v(-3.83, -26.76) * mm, "end": v(-3.83, -26.24) * mm});
            skLineSegment(sketch, "E276", {"start": v(-3.37, -26.85) * mm, "end": v(-3.83, -26.76) * mm});
            skLineSegment(sketch, "E277", {"start": v(-3.37, -28.86) * mm, "end": v(-3.37, -26.85) * mm});
            skLineSegment(sketch, "E278", {"start": v(-3.79, -28.95) * mm, "end": v(-3.37, -28.86) * mm});
            skLineSegment(sketch, "E279", {"start": v(-6.22, -28.8) * mm, "end": v(-6.07, -28.88) * mm});
            skLineSegment(sketch, "E280", {"start": v(-6.07, -28.88) * mm, "end": v(-5.92, -28.9) * mm});
            skSolve(sketch);
        }
        {
            var Q0;
            Q0 = qSketchRegion(id + "F6", true);
            extrude(context, id + "F7", {"entities" : qUnion([Q0]), "operationType" : NewBodyOperationType.ADD, "depth" : 2 * mm, "offsetDistance" : 25 * mm});
        }
    });
